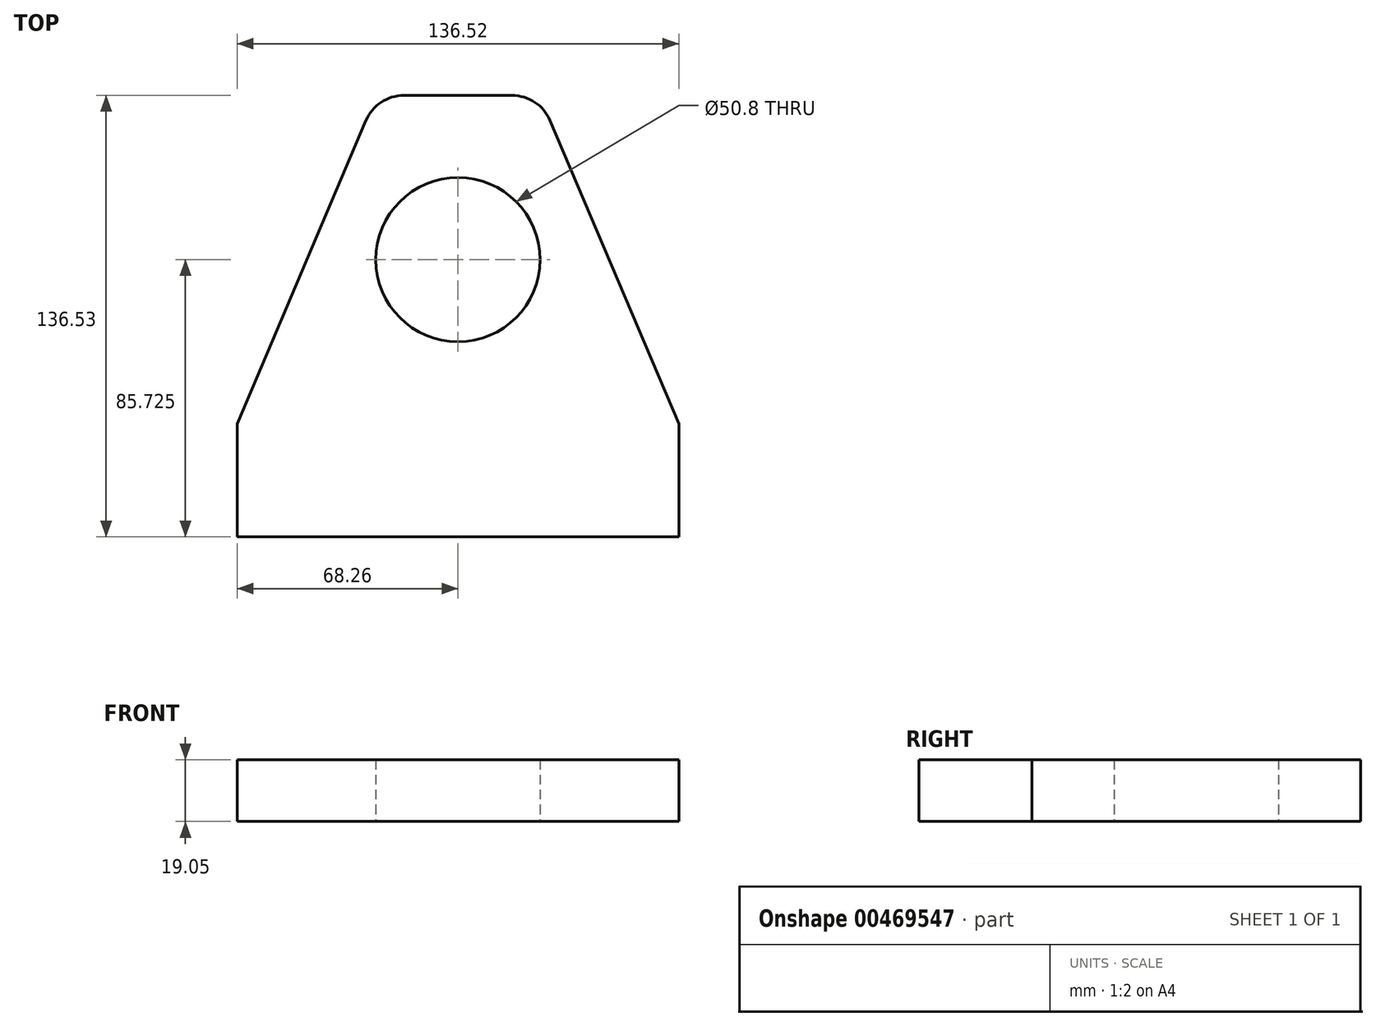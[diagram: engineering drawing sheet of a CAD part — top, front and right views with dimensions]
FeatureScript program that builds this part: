
annotation { "Feature Type Name" : "Feature", "Feature Type Description" : "" }
export const myFeature = defineFeature(function(context is Context, id is Id, definition is map)
    precondition{}
    {
        {
            var Q0;
            Q0=qCreatedBy(makeId("Top.planeOp"),FACE);
            var sketch = newSketch(context, id + "F0", { "sketchPlane" : qUnion([Q0])});
            skLineSegment(sketch, "E0", {"start": v(-68.26, 0) * mm, "end": v(68.26, 0) * mm});
            skLineSegment(sketch, "E1", {"start": v(68.26, 0) * mm, "end": v(68.26, 34.92) * mm});
            skLineSegment(sketch, "E2", {"start": v(68.26, 34.93) * mm, "end": v(28.42, 128.79) * mm});
            skLineSegment(sketch, "E3", {"start": v(16.73, 136.53) * mm, "end": v(-16.73, 136.53) * mm});
            skLineSegment(sketch, "E4", {"start": v(-28.42, 128.79) * mm, "end": v(-68.26, 34.92) * mm});
            skLineSegment(sketch, "E5", {"start": v(-68.26, 34.92) * mm, "end": v(-68.26, 0) * mm});
            skCircle(sketch, "E6", {"center": v(0, 85.73) * mm, "radius": 25.4 * mm});
            skPoint(sketch, "E7.visualSharp", {"position": v(-25.14, 136.53) * mm});
            skArc(sketch, "E7.filletArc", {"start": v(-16.73, 136.52) * mm, "mid": v(-23.74, 134.42) * mm, "end": v(-28.42, 128.79) * mm});
            skPoint(sketch, "E8.visualSharp", {"position": v(25.14, 136.53) * mm});
            skArc(sketch, "E8.filletArc", {"start": v(28.42, 128.79) * mm, "mid": v(23.74, 134.42) * mm, "end": v(16.73, 136.53) * mm});
            skSolve(sketch);
        }
        {
            var Q0;
            Q0 = qSketchRegion(id + "F0", true);
            extrude(context, id + "F1", {"entities" : qUnion([Q0]), "depth" : 19.05 * mm, "offsetDistance" : 25.4 * mm});
        }
    });
